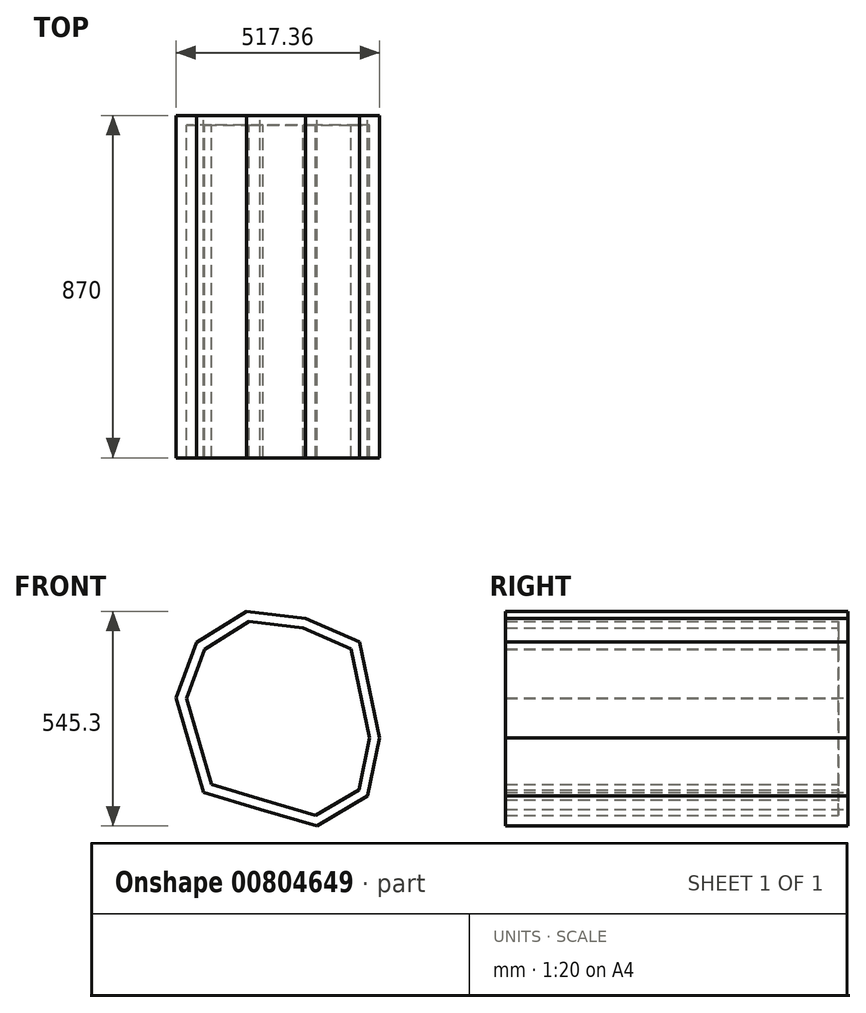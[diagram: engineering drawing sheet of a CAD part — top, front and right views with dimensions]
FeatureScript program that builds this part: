
annotation { "Feature Type Name" : "Feature", "Feature Type Description" : "" }
export const myFeature = defineFeature(function(context is Context, id is Id, definition is map)
    precondition{}
    {
        {
            var Q0;
            Q0=qCreatedBy(makeId("Front.planeOp"),FACE);
            var sketch = newSketch(context, id + "F0", { "sketchPlane" : qUnion([Q0])});
            skLineSegment(sketch, "E0.0", {"start": v(263.95, 122.34) * mm, "end": v(315.27, -122.34) * mm});
            skLineSegment(sketch, "E0.1", {"start": v(315.27, -122.34) * mm, "end": v(284.67, -269.18) * mm});
            skLineSegment(sketch, "E0.2", {"start": v(284.67, -269.18) * mm, "end": v(155.66, -345.71) * mm});
            skLineSegment(sketch, "E0.3", {"start": v(155.66, -345.71) * mm, "end": v(11.64, -303.8) * mm});
            skLineSegment(sketch, "E0.4", {"start": v(11.64, -303.8) * mm, "end": v(-131.93, -260.34) * mm});
            skLineSegment(sketch, "E0.5", {"start": v(-131.93, -260.34) * mm, "end": v(-202.09, -20.39) * mm});
            skLineSegment(sketch, "E0.6", {"start": v(-202.09, -20.39) * mm, "end": v(-149.87, 120.23) * mm});
            skLineSegment(sketch, "E0.7", {"start": v(-149.87, 120.23) * mm, "end": v(-22.58, 199.59) * mm});
            skLineSegment(sketch, "E0.8", {"start": v(-22.58, 199.59) * mm, "end": v(126.4, 182.18) * mm});
            skLineSegment(sketch, "E0.9", {"start": v(126.4, 182.18) * mm, "end": v(263.95, 122.34) * mm});
            skPoint(sketch, "E0.0.midPoint", {"position": v(289.6, 0) * mm});
            skPoint(sketch, "E0.cCircle.center.orphan", {"position": v(0, 0) * mm});
            skSolve(sketch);
        }
        {
            var Q0;
            Q0 = qSketchRegion(id + "F0", true);
            extrude(context, id + "F1", {"entities" : qUnion([Q0]), "depth" : 870 * mm, "offsetDistance" : 25 * mm});
        }
        {
            var Q0;
            Q0=makeQuery(id+"F1.opExtrude","CAP_FACE",FACE,{"disambiguationData":[OSD([sQuery(id+"F0.wireOp",EDGE,"E0.0"),sQuery(id+"F0.wireOp",EDGE,"E0.1"),sQuery(id+"F0.wireOp",EDGE,"E0.2"),sQuery(id+"F0.wireOp",EDGE,"E0.3"),sQuery(id+"F0.wireOp",EDGE,"E0.4"),sQuery(id+"F0.wireOp",EDGE,"E0.5"),sQuery(id+"F0.wireOp",EDGE,"E0.6"),sQuery(id+"F0.wireOp",EDGE,"E0.7"),sQuery(id+"F0.wireOp",EDGE,"E0.8"),sQuery(id+"F0.wireOp",EDGE,"E0.9")])],"isStart":false});
            shell(context, id + "F2", {"entities" : qUnion([Q0]), "thickness" : 25 * mm});
        }
    });
